# Revit family: СМ-ВО
name_source: partatom
category: Арматура воздуховодов
units: mm (PartAtom-declared; Revit-internal decimal feet)

## family parameters
Всегда вертикально = Да
На основе рабочей плоскости = Нет
Общий = Нет
При загрузке вырезать с полостями = Нет
Размер круглого соединителя = Использовать диаметр
Тип детали = Присоединяется

## types (8) — shared parameters
00_20_Manufacturer = Вентс
00_20_Name = Монтажний стакан
Casing Material = Условный материал-отделка
Grid Material = Условный материал-отделка
Load Classification = HVAC
Maintenance zone material = <По категории>
zero-valued in all types: Отметка по умолчанию

## per-type parameters (varying)
| type | A | B | C | D | Dy | Вес | Косынка | Фаска |
| СМ-ВО-0010-315/355 | 480 мм | 590 мм | 800 мм | 505 мм | 500 мм | 43.5 кг | 400 мм | 126 мм |
| СМ-ВО-0010-400/450 | 580 мм | 692 мм | 900 мм | 605 мм | 600 мм | 51.5 кг | 500 мм | 151 мм |
| СМ-ВО-0010-500 | 640 мм | 760 мм | 970 мм | 675 мм | 670 мм | 56 кг | 570 мм | 169 мм |
| СМ-ВО-0010-560/630 | 750 мм | 910 мм | 1120 мм | 835 мм | 830 мм | 66.5 кг | 730 мм | 209 мм |
| СМ-ВО-0010-710/800 | 980 мм | 1140 мм | 1350 мм | 1055 мм | 1050 мм | 83 кг | 950 мм | 264 мм |
| СМ-ВО-0010-900 | 1050 мм | 1208 мм | 1420 мм | 1105 мм | 1100 мм | 88.5 кг | 1000 мм | 276 мм |
| СМ-ВО-0010-1000/1120 | 1340 мм | 1498 мм | 1710 мм | 1405 мм | 1400 мм | 112 кг | 1300 мм | 351 мм |
| СМ-ВО-0010-1250 | 1500 мм | 1688 мм | 1900 мм | 1605 мм | 1600 мм | 151 кг | 1500 мм | 401 мм |

note: column(s) folded — value = type name in every type: 00_20_Type
